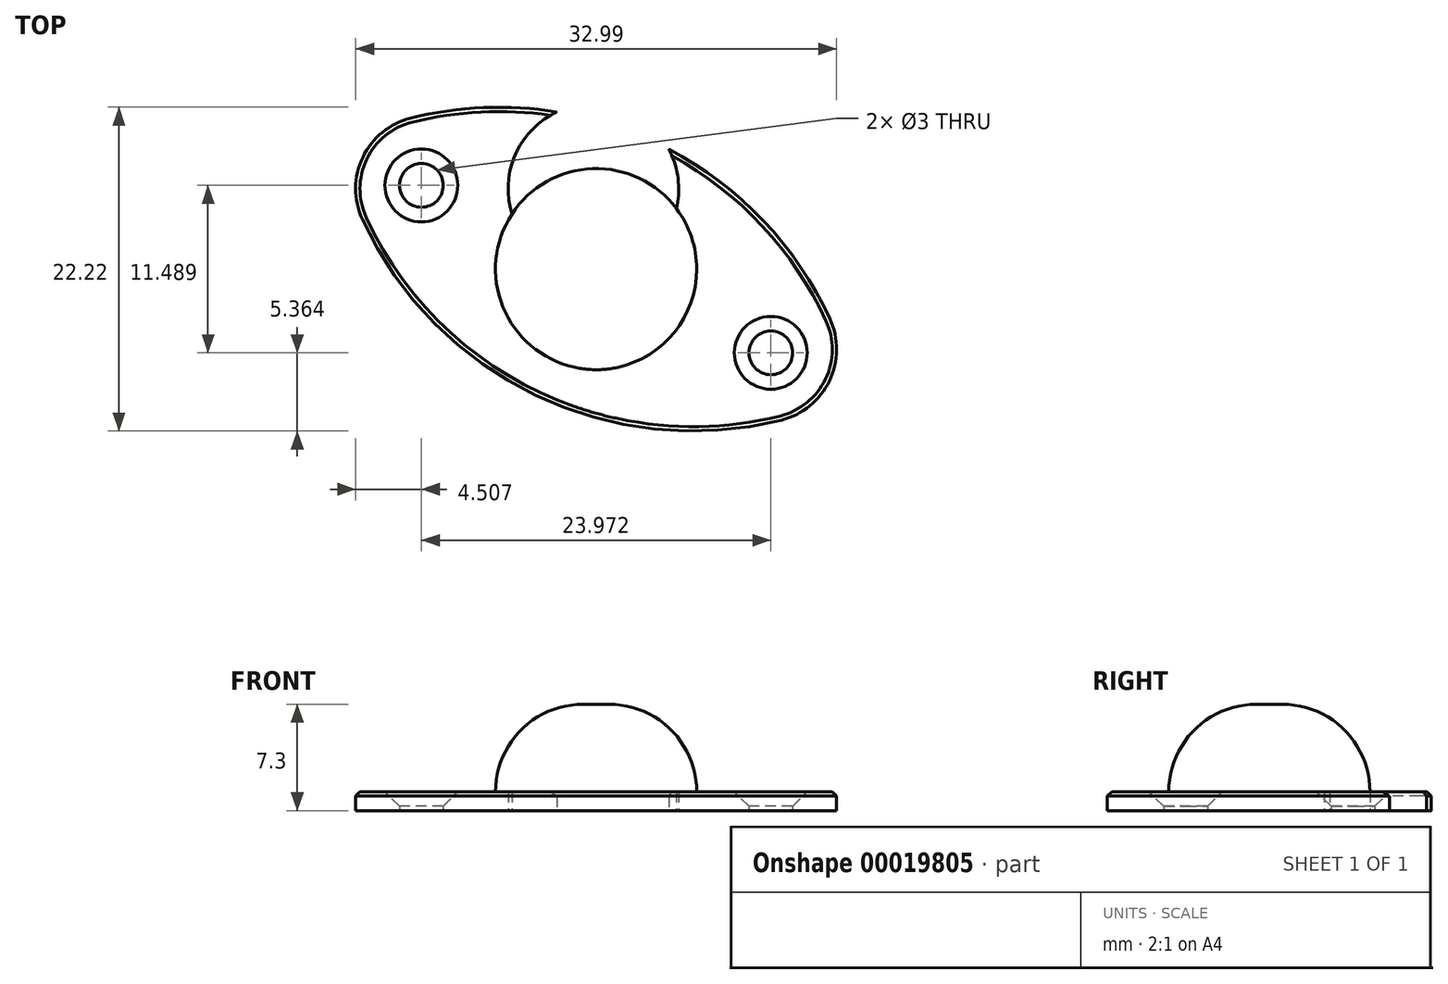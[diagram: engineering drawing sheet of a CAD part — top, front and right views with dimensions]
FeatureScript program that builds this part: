
annotation { "Feature Type Name" : "Feature", "Feature Type Description" : "" }
export const myFeature = defineFeature(function(context is Context, id is Id, definition is map)
    precondition{}
    {
        {
            var Q0;
            Q0=qCreatedBy(makeId("Top.planeOp"),FACE);
            var sketch = newSketch(context, id + "F0", { "sketchPlane" : qUnion([Q0])});
            skArc(sketch, "E0", {"start": v(-25.45, 16.02) * mm, "mid": v(-37.34, 28.1) * mm, "end": v(-54.2, 29.8) * mm});
            skLineSegment(sketch, "E1", {"start": v(-59.24, 27.95) * mm, "end": v(-23.74, 10.93) * mm, "construction": true});
            skArc(sketch, "E2.0.MirrorCS", {"start": v(-28.78, 9.08) * mm, "mid": v(-45.63, 10.79) * mm, "end": v(-57.53, 22.86) * mm});
            skCircle(sketch, "E3", {"center": v(-41.49, 19.44) * mm, "radius": 6.9 * mm});
            skLineSegment(sketch, "E4", {"start": v(-59.24, 27.95) * mm, "end": v(-47.7, 22.42) * mm, "construction": true});
            skCircle(sketch, "E5", {"center": v(-53.47, 25.18) * mm, "radius": 1.5 * mm});
            skLineSegment(sketch, "E6", {"start": v(-34.84, 33.32) * mm, "end": v(-48.14, 5.56) * mm, "construction": true});
            skCircle(sketch, "E7.0.MirrorC", {"center": v(-29.5, 13.7) * mm, "radius": 1.5 * mm});
            skCircle(sketch, "E8", {"center": v(-41.49, 19.44) * mm, "radius": 5.85 * mm});
            skPoint(sketch, "E9.visualSharp", {"position": v(-59.24, 27.95) * mm});
            skArc(sketch, "E9.filletArc", {"start": v(-54.2, 29.8) * mm, "mid": v(-57.5, 27.11) * mm, "end": v(-57.53, 22.86) * mm});
            skPoint(sketch, "E10.visualSharp", {"position": v(-23.74, 10.93) * mm});
            skArc(sketch, "E10.filletArc", {"start": v(-28.78, 9.08) * mm, "mid": v(-25.48, 11.77) * mm, "end": v(-25.45, 16.02) * mm});
            skSolve(sketch);
        }
        {
            var Q0;
            Q0=makeQuery(id+"F0.imprint","IMPRINT",FACE,{"disambiguationData":[TD([[makeQuery(id+"F0.imprint","IMPRINT",EDGE,{"derivedFrom":sQuery(id+"F0.wireOp",EDGE,"E0")}),1.0]])]});
            extrude(context, id + "F1", {"entities" : qUnion([Q0]), "depth" : 1.3 * mm});
        }
        {
            var Q0;
            Q0=makeQuery(id+"F1.opExtrude","CAP_EDGE",EDGE,{"disambiguationData":[OSD([sQuery(id+"F0.wireOp",EDGE,"E5")])],"isStart":false});
            var Q1;
            Q1=makeQuery(id+"F1.opExtrude","CAP_EDGE",EDGE,{"disambiguationData":[OSD([sQuery(id+"F0.wireOp",EDGE,"E7.0.MirrorC")])],"isStart":false});
            chamfer(context, id + "F2", {"entities" : qUnion([Q0, Q1]), "chamferType" : ChamferType.OFFSET_ANGLE, "width" : 1 * mm, "oppositeDirection" : false, "angle" : 45 * degree, "tangentPropagation" : true});
        }
        {
            var Q0;
            Q0=makeQuery(id+"F1.opExtrude","CAP_EDGE",EDGE,{"disambiguationData":[OSD([sQuery(id+"F0.wireOp",EDGE,"E2.0.MirrorCS")])],"isStart":false});
            var Q1;
            Q1=makeQuery(id+"F1.opExtrude","CAP_EDGE",EDGE,{"disambiguationData":[OSD([sQuery(id+"F0.wireOp",EDGE,"E0")])],"isStart":false});
            chamfer(context, id + "F3", {"entities" : qUnion([Q0, Q1]), "width" : .3 * mm, "tangentPropagation" : true});
        }
        {
            var Q0;
            Q0=makeQuery(id+"F0.imprint","IMPRINT",FACE,{"disambiguationData":[TD([[makeQuery(id+"F0.imprint","IMPRINT",EDGE,{"derivedFrom":sQuery(id+"F0.wireOp",EDGE,"E8")}),1.0]])]});
            var Q1;
            Q1=makeQuery(id+"F0.imprint","IMPRINT",FACE,{"disambiguationData":[TD([[makeQuery(id+"F0.imprint","IMPRINT",EDGE,{"derivedFrom":sQuery(id+"F0.wireOp",EDGE,"E3")}),1.0]])]});
            extrude(context, id + "F4", {"entities" : qUnion([Q0, Q1]), "operationType" : NewBodyOperationType.ADD, "depth" : 7.3 * mm});
        }
        {
            var Q0;
            Q0=makeQuery(id+"F4.opExtrude","CAP_FACE",FACE,{"disambiguationData":[OSD([sQuery(id+"F0.wireOp",EDGE,"E3")])],"isStart":false});
            fillet(context, id + "F5", {"entities" : qUnion([Q0]), "radius" : 6 * mm, "tangentPropagation" : true, "allowEdgeOverflow" : false});
        }
        {
            var Q0;
            Q0=qCreatedBy(makeId("Front.planeOp"),FACE);
            var sketch = newSketch(context, id + "F6", { "sketchPlane" : qUnion([Q0])});
            skLineSegment(sketch, "E11", {"start": v(-43.01, 1.3) * mm, "end": v(-40.01, 1.3) * mm});
            skFitSpline(sketch, "E12", {"points": [v(-43.01, 1.3) * mm, v(-41.54, 5.5) * mm, v(-40.01, 1.3) * mm], "startDerivative": vector(-1.89, 10.57) * mm, "endDerivative": vector(-2.73, -10.51) * mm});
            skSolve(sketch);
        }
        {
            var Q0;
            Q0=makeQuery(id+"F0.imprint","IMPRINT",FACE,{"disambiguationData":[TD([[makeQuery(id+"F0.imprint","IMPRINT",EDGE,{"derivedFrom":sQuery(id+"F0.wireOp",EDGE,"E8")}),1.0]])]});
            var sketch = newSketch(context, id + "F7", { "sketchPlane" : qUnion([Q0])});
            skCircle(sketch, "E13", {"center": v(-41.67, 24.94) * mm, "radius": 5.85 * mm});
            skSolve(sketch);
        }
        {
            var Q0;
            Q0=qSketchRegion(id+"F7",true);
            var Q1;
            Q1=makeQuery(id+"F4.opExtrude","CAP_FACE",FACE,{"disambiguationData":[OSD([sQuery(id+"F0.wireOp",EDGE,"E3")])],"isStart":false});
            extrude(context, id + "F8", {"entities" : qUnion([Q0]), "operationType" : NewBodyOperationType.REMOVE, "endBound" : BoundingType.SYMMETRIC, "endBoundEntity" : qUnion([Q1]), "depth" : 8 * mm});
        }
        {
            var Q0;
            Q0=makeQuery(id+"F6.imprint","IMPRINT",FACE,{"disambiguationData":[TD([[makeQuery(id+"F6.imprint","IMPRINT",EDGE,{"derivedFrom":sQuery(id+"F6.wireOp",EDGE,"E11")}),1.0]])]});
            extrude(context, id + "F9", {"entities" : qUnion([Q0]), "operationType" : NewBodyOperationType.REMOVE, "oppositeDirection" : true, "depth" : 30 * mm});
        }
        {
            var Q0;
            Q0=makeQuery(id+"F0.imprint","IMPRINT",FACE,{"disambiguationData":[TD([[makeQuery(id+"F0.imprint","IMPRINT",EDGE,{"derivedFrom":sQuery(id+"F0.wireOp",EDGE,"E3")}),1.0]])]});
            var Q1;
            Q1=makeQuery(id+"F0.imprint","IMPRINT",FACE,{"disambiguationData":[TD([[makeQuery(id+"F0.imprint","IMPRINT",EDGE,{"derivedFrom":sQuery(id+"F0.wireOp",EDGE,"E8")}),1.0]])]});
            var Q2;
            Q2=sQuery(id+"F0.wireOp",EDGE,"E3");
            extrude(context, id + "F10", {"entities" : qUnion([Q0, Q1]), "operationType" : NewBodyOperationType.ADD, "surfaceEntities" : qUnion([Q2]), "depth" : 7.3 * mm});
        }
        {
            var Q0;
            Q0=makeQuery(id+"F10.opExtrude","CAP_FACE",FACE,{"disambiguationData":[OSD([sQuery(id+"F0.wireOp",EDGE,"E3")])],"isStart":false});
            fillet(context, id + "F11", {"entities" : qUnion([Q0]), "radius" : 6 * mm, "tangentPropagation" : true, "allowEdgeOverflow" : false});
        }
    });
